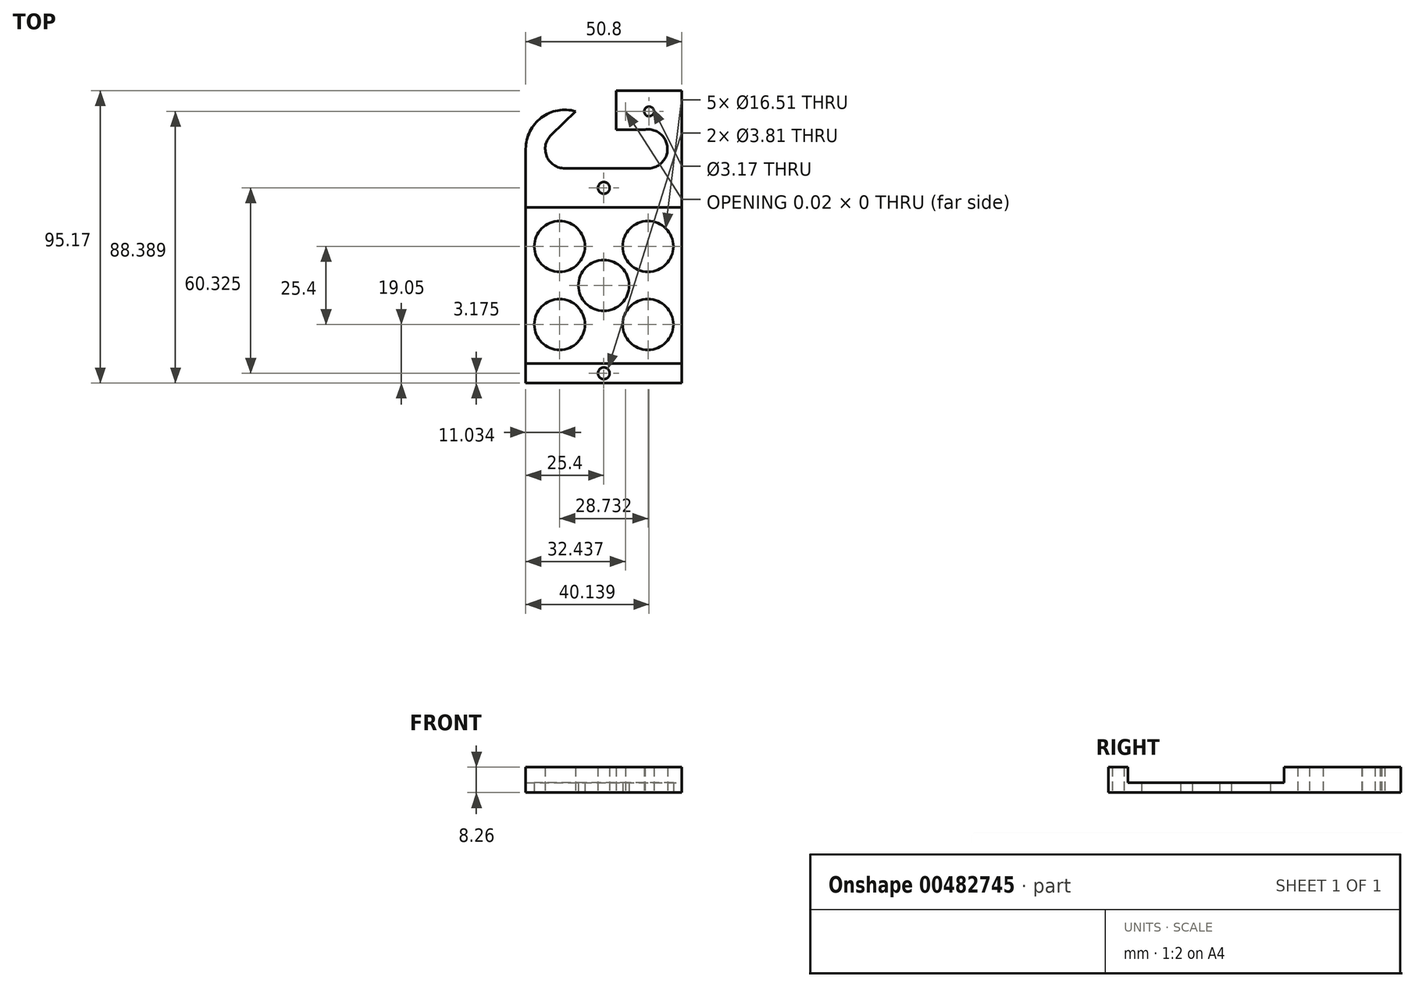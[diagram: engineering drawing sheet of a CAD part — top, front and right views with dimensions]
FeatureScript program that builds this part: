
annotation { "Feature Type Name" : "Feature", "Feature Type Description" : "" }
export const myFeature = defineFeature(function(context is Context, id is Id, definition is map)
    precondition{}
    {
        {
            var Q0;
            Q0=qCreatedBy(makeId("Top.planeOp"),FACE);
            var sketch = newSketch(context, id + "F0", { "sketchPlane" : qUnion([Q0])});
            skLineSegment(sketch, "E0", {"start": v(-41.14, 0) * mm, "end": v(38.9, 0) * mm, "construction": true});
            skLineSegment(sketch, "E1", {"start": v(0, 39.41) * mm, "end": v(0, -31.75) * mm, "construction": true});
            skLineSegment(sketch, "E2.0", {"start": v(-41.14, -25.4) * mm, "end": v(38.9, -25.4) * mm, "construction": true});
            skLineSegment(sketch, "E3.MirrorCS", {"start": v(-41.14, 25.4) * mm, "end": v(38.9, 25.4) * mm, "construction": true});
            skLineSegment(sketch, "E4.0", {"start": v(-25.4, 44.45) * mm, "end": v(-25.4, -31.75) * mm, "construction": true});
            skLineSegment(sketch, "E5.MirrorCS", {"start": v(25.4, 39.41) * mm, "end": v(25.4, -31.75) * mm, "construction": true});
            skLineSegment(sketch, "E6.0", {"start": v(-41.14, -31.75) * mm, "end": v(38.9, -31.75) * mm, "construction": true});
            skLineSegment(sketch, "E7.0", {"start": v(-41.14, 31.75) * mm, "end": v(38.9, 31.75) * mm, "construction": true});
            skLineSegment(sketch, "E8.0", {"start": v(14.37, 54.16) * mm, "end": v(14.37, -26.9) * mm, "construction": true});
            skLineSegment(sketch, "E9.0", {"start": v(-25.4, 44.45) * mm, "end": v(14.37, 44.45) * mm, "construction": true});
            skPoint(sketch, "E10.orphan", {"position": v(-25.4, 39.41) * mm});
            skPoint(sketch, "E11.orphan", {"position": v(25.4, -26.9) * mm});
            skPoint(sketch, "E12.orphan", {"position": v(-25.4, -26.9) * mm});
            skLineSegment(sketch, "E13.top", {"start": v(-25.4, -31.75) * mm, "end": v(25.4, -31.75) * mm});
            skLineSegment(sketch, "E13.left", {"start": v(-25.4, 44.45) * mm, "end": v(-25.4, -31.75) * mm});
            skLineSegment(sketch, "E13.right", {"start": v(25.4, 44.45) * mm, "end": v(25.4, -31.75) * mm});
            skArc(sketch, "E14", {"start": v(-9.13, 56.64) * mm, "mid": v(-20.32, 54.61) * mm, "end": v(-25.4, 44.45) * mm});
            skLineSegment(sketch, "E15.0", {"start": v(-17.09, 49.04) * mm, "end": v(-9.13, 56.64) * mm});
            skArc(sketch, "E16", {"start": v(-17.09, 49.04) * mm, "mid": v(-18.6, 42.09) * mm, "end": v(-12.7, 38.1) * mm});
            skLineSegment(sketch, "E17.trimOffspring", {"start": v(-3.37, 44.45) * mm, "end": v(0, 44.45) * mm});
            skLineSegment(sketch, "E18", {"start": v(25.4, 56.64) * mm, "end": v(25.4, 44.45) * mm});
            skCircle(sketch, "E19", {"center": v(0, 31.75) * mm, "radius": 1.9 * mm});
            skLineSegment(sketch, "E20.0", {"start": v(-41.14, -28.58) * mm, "end": v(38.9, -28.58) * mm, "construction": true});
            skCircle(sketch, "E21", {"center": v(0, -28.58) * mm, "radius": 1.9 * mm});
            skLineSegment(sketch, "E22", {"start": v(-25.4, 25.4) * mm, "end": v(25.4, 25.4) * mm});
            skLineSegment(sketch, "E23", {"start": v(25.4, -25.4) * mm, "end": v(-25.4, -25.4) * mm});
            skLineSegment(sketch, "E24", {"start": v(-12.7, 38.1) * mm, "end": v(14.37, 38.1) * mm});
            skLineSegment(sketch, "E25", {"start": v(-12.7, 44.45) * mm, "end": v(-12.7, 50.72) * mm, "construction": true});
            skLineSegment(sketch, "E26", {"start": v(-12.7, 50.72) * mm, "end": v(4.08, 50.72) * mm, "construction": true});
            skArc(sketch, "E27", {"start": v(14.37, 38.1) * mm, "mid": v(20.7, 44.96) * mm, "end": v(13.36, 50.72) * mm});
            skLineSegment(sketch, "E28", {"start": v(4.08, 50.72) * mm, "end": v(13.36, 50.72) * mm});
            skLineSegment(sketch, "E29", {"start": v(-9.13, 56.64) * mm, "end": v(4.08, 56.64) * mm, "construction": true});
            skPoint(sketch, "E30.orphan", {"position": v(25.4, 54.16) * mm});
            skLineSegment(sketch, "E31", {"start": v(7.05, 56.64) * mm, "end": v(7.03, 56.64) * mm});
            skLineSegment(sketch, "E32.MirrorCS", {"start": v(-14.37, 54.16) * mm, "end": v(-14.37, -26.9) * mm, "construction": true});
            skLineSegment(sketch, "E33.0", {"start": v(-41.14, -12.7) * mm, "end": v(38.9, -12.7) * mm, "construction": true});
            skLineSegment(sketch, "E34.MirrorCS", {"start": v(-41.14, 12.7) * mm, "end": v(38.9, 12.7) * mm, "construction": true});
            skCircle(sketch, "E35", {"center": v(-14.37, 12.7) * mm, "radius": 8.26 * mm});
            skCircle(sketch, "E36", {"center": v(14.37, 12.7) * mm, "radius": 8.26 * mm});
            skCircle(sketch, "E37", {"center": v(-14.37, -12.7) * mm, "radius": 8.26 * mm});
            skCircle(sketch, "E38", {"center": v(14.37, -12.7) * mm, "radius": 8.26 * mm});
            skCircle(sketch, "E39", {"center": v(0, 0) * mm, "radius": 8.26 * mm});
            skLineSegment(sketch, "E40", {"start": v(7.04, 53.68) * mm, "end": v(7.05, 53.68) * mm});
            skArc(sketch, "E41", {"start": v(7.05, 56.64) * mm, "mid": v(7.04, 56.64) * mm, "end": v(7.03, 56.64) * mm});
            skLineSegment(sketch, "E42.trimOffspring", {"start": v(7.03, 50.72) * mm, "end": v(25.4, 50.72) * mm, "construction": true});
            skPoint(sketch, "E43.orphan", {"position": v(4.08, 53.68) * mm});
            skArc(sketch, "E44.trimOffspring", {"start": v(7.03, 50.72) * mm, "mid": v(7.04, 50.72) * mm, "end": v(7.05, 50.72) * mm});
            skPoint(sketch, "E45.end.orphan", {"position": v(14.37, 55.1) * mm});
            skPoint(sketch, "E45.start.orphan", {"position": v(7.05, 55.1) * mm});
            skLineSegment(sketch, "E46", {"start": v(4.08, 50.72) * mm, "end": v(4.08, 63.42) * mm});
            skLineSegment(sketch, "E47", {"start": v(4.08, 63.42) * mm, "end": v(12.38, 63.42) * mm});
            skLineSegment(sketch, "E48", {"start": v(25.4, 63.42) * mm, "end": v(25.4, 56.64) * mm});
            skLineSegment(sketch, "E49", {"start": v(4.08, 56.64) * mm, "end": v(25.4, 56.64) * mm, "construction": true});
            skArc(sketch, "E50", {"start": v(13.8, 57.93) * mm, "mid": v(14.74, 55.05) * mm, "end": v(15.67, 57.93) * mm});
            skLineSegment(sketch, "E51", {"start": v(14.74, 56.64) * mm, "end": v(14.74, 63.42) * mm, "construction": true});
            skLineSegment(sketch, "E52.0", {"start": v(16.52, 56.64) * mm, "end": v(16.52, 63.42) * mm, "construction": true});
            skLineSegment(sketch, "E53.MirrorCS", {"start": v(12.96, 56.64) * mm, "end": v(12.96, 63.42) * mm, "construction": true});
            skLineSegment(sketch, "E54.trimOffspring", {"start": v(12.96, 63.42) * mm, "end": v(25.4, 63.42) * mm});
            skLineSegment(sketch, "E55.trimOffspring", {"start": v(12.38, 63.42) * mm, "end": v(12.96, 63.42) * mm});
            skPoint(sketch, "E56.orphan", {"position": v(16.52, 63.42) * mm});
            skArc(sketch, "E57", {"start": v(13.8, 57.93) * mm, "mid": v(14.74, 58.23) * mm, "end": v(15.67, 57.93) * mm});
            skSolve(sketch);
        }
        {
            var Q0;
            {var subQ0=sQuery(id+"F0.wireOp",EDGE,"E22");Q0=makeQuery(id+"F0.imprint","IMPRINT",FACE,{"disambiguationData":[TD([[makeQuery(id+"F0.imprint","IMPRINT",EDGE,{"derivedFrom":subQ0}),-1.0]])]});}
            extrude(context, id + "F1", {"entities" : qUnion([Q0]), "depth" : 3.17 * mm});
        }
        {
            var Q0;
            {var subQ2=sQuery(id+"F0.wireOp",EDGE,"E14");Q0=makeQuery(id+"F0.imprint","IMPRINT",FACE,{"disambiguationData":[TD([[makeQuery(id+"F0.imprint","IMPRINT",EDGE,{"derivedFrom":subQ2}),1.0]])]});}
            var Q1;
            {var subQ1=sQuery(id+"F0.wireOp",EDGE,"E13.top");Q1=makeQuery(id+"F0.imprint","IMPRINT",FACE,{"disambiguationData":[TD([[makeQuery(id+"F0.imprint","IMPRINT",EDGE,{"derivedFrom":subQ1}),1.0]])]});}
            extrude(context, id + "F2", {"entities" : qUnion([Q0, Q1]), "operationType" : NewBodyOperationType.ADD, "depth" : 8.25 * mm});
        }
    });
